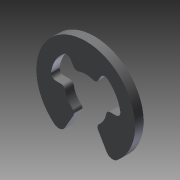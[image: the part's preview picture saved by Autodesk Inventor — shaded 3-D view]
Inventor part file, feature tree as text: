
AUTODESK INVENTOR PART (.ipt)
format: ipt  version: 2012 (Build 160160000, 160)  size: 117,248 bytes
history: native  units: in
note: dims shown in document units (in); Inventor stores cm internally (conversion verified against a paired STEP export)
features: other x7, extrude x1, sketch x1
ambient origin geometry x8: Origin, YZ Plane, XZ Plane, XY Plane, X Axis, Y Axis, Z Axis, Center Point
bodies: Solid1 (feature_tree)
feature tree (9):
  extrude  "Extrusion1"  [1 undecoded]
  other  "RR_XY"
  other  "RR_YZ"
  other  "RR_ZX"
  other  "RR_X"
  other  "RR_Y"
  other  "RR_Z"
  other  "RR_Center"
  sketch  "Sketch_1"  dims[d0=0.0435in d1=0.0in]
note: 1 required parameter value undecoded (feature->parameter linkage not recoverable at this tier; creation-order binding heuristic only, values carry confidence <= 0.55)
